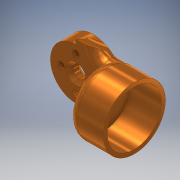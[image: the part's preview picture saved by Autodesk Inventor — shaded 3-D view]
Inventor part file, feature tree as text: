
AUTODESK INVENTOR PART (.ipt)
format: ipt  version: 2017 SP1 (Build 210196100, 196)  size: 448,512 bytes
history: native  units: mm
features: extrude x7, sketch x7, chamfer x3, fillet x3
ambient origin geometry x8: Origin, YZ Plane, XZ Plane, XY Plane, X Axis, Y Axis, Z Axis, Center Point
bodies: Solid1 (feature_tree)
feature tree (20):
  extrude  "Extrusion1"  Depth=34.0mm
  extrude  "Extrusion2"  Depth=20.0mm TaperAngle=0.0deg
  extrude  "Extrusion3"  Depth=3.6mm
  extrude  "Extrusion4"  Depth=3.6mm
  extrude  "Extrusion5"  Depth=25.5mm TaperAngle=0.0deg
  extrude  "Extrusion6"  Depth=17.5mm TaperAngle=0.0deg
  chamfer  "Chamfer1"  Distance=13.0mm
  fillet  "Fillet1"  Radius=7.0mm
  fillet  "Fillet2"  Radius=16.0mm
  chamfer  "Chamfer2"  Distance=19.0mm
  extrude  "Extrusion7"  Depth=1.6mm
  fillet  "Fillet3"  Radius=3.6mm
  chamfer  "Chamfer3"  Distance=3.6mm
  sketch  "Sketch1"  dims[d0=29.7mm d1=34.0mm]
  sketch  "Sketch2"  dims[d2=17.0mm d3=0.0mm d4=20.0mm d5=0.0mm]
  sketch  "Sketch3"  dims[d6=12.0mm d7=3.6mm]
  sketch  "Sketch4"  dims[d8=3.6mm d9=3.6mm]
  sketch  "Sketch5"  dims[d10=3.6mm d11=25.5mm d12=0.0mm]
  sketch  "Sketch6"  dims[d13=5.0mm d14=17.5mm d15=0.0mm]
  sketch  "Sketch7"  dims[d16=28.0mm d17=13.0mm d18=0.0mm d19=7.0mm d20=16.0mm d21=19.0mm d22=3.6mm d23=3.6mm d24=3.6mm d25=3.6mm d26=15.0mm d27=0.0mm d28=3.0mm d29=2.0mm d30=45.0deg d31=8.0mm d32=5.0mm d33=2.0mm d34=2.0mm d35=45.0deg d36=6.0mm d37=0.0mm d38=1.6mm d39=2.0mm d40=2.0mm d41=45.0deg]
